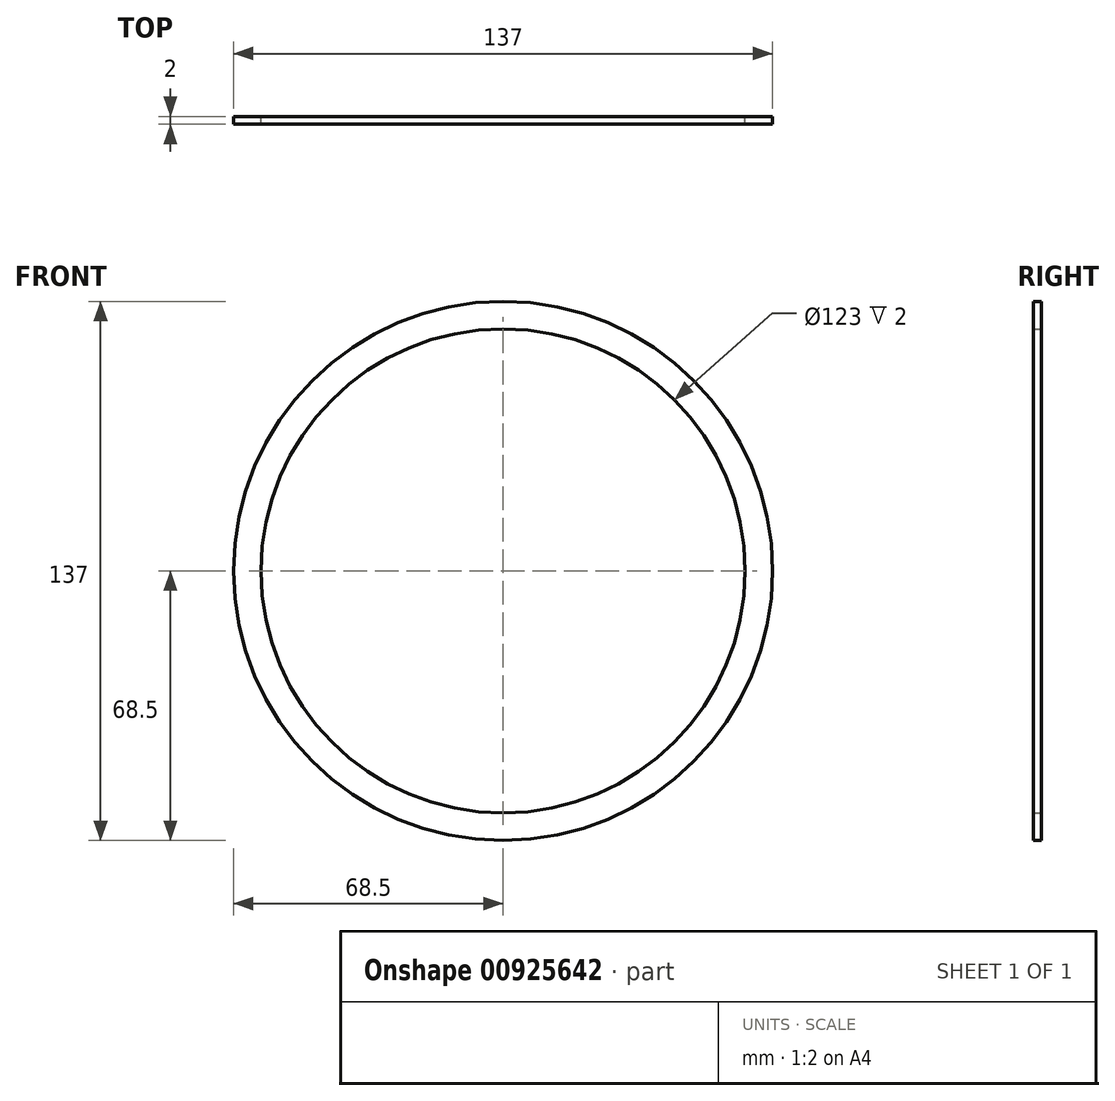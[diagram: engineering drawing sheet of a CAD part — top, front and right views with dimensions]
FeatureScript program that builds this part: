
annotation { "Feature Type Name" : "Feature", "Feature Type Description" : "" }
export const myFeature = defineFeature(function(context is Context, id is Id, definition is map)
    precondition{}
    {
        {
            var Q0;
            Q0=qCreatedBy(makeId("Front.planeOp"),FACE);
            var sketch = newSketch(context, id + "F0", { "sketchPlane" : qUnion([Q0])});
            skCircle(sketch, "E0", {"center": v(0, 0) * mm, "radius": 68.5 * mm});
            skCircle(sketch, "E1", {"center": v(0, 0) * mm, "radius": 61.5 * mm});
            skSolve(sketch);
        }
        {
            var Q0;
            Q0=makeQuery(id+"F0.imprint","IMPRINT",FACE,{"disambiguationData":[TD([[makeQuery(id+"F0.imprint","IMPRINT",EDGE,{"derivedFrom":sQuery(id+"F0.wireOp",EDGE,"E0")}),1.0]])]});
            extrude(context, id + "F1", {"entities" : qUnion([Q0]), "depth" : 2 * mm, "offsetDistance" : 25 * mm});
        }
    });
